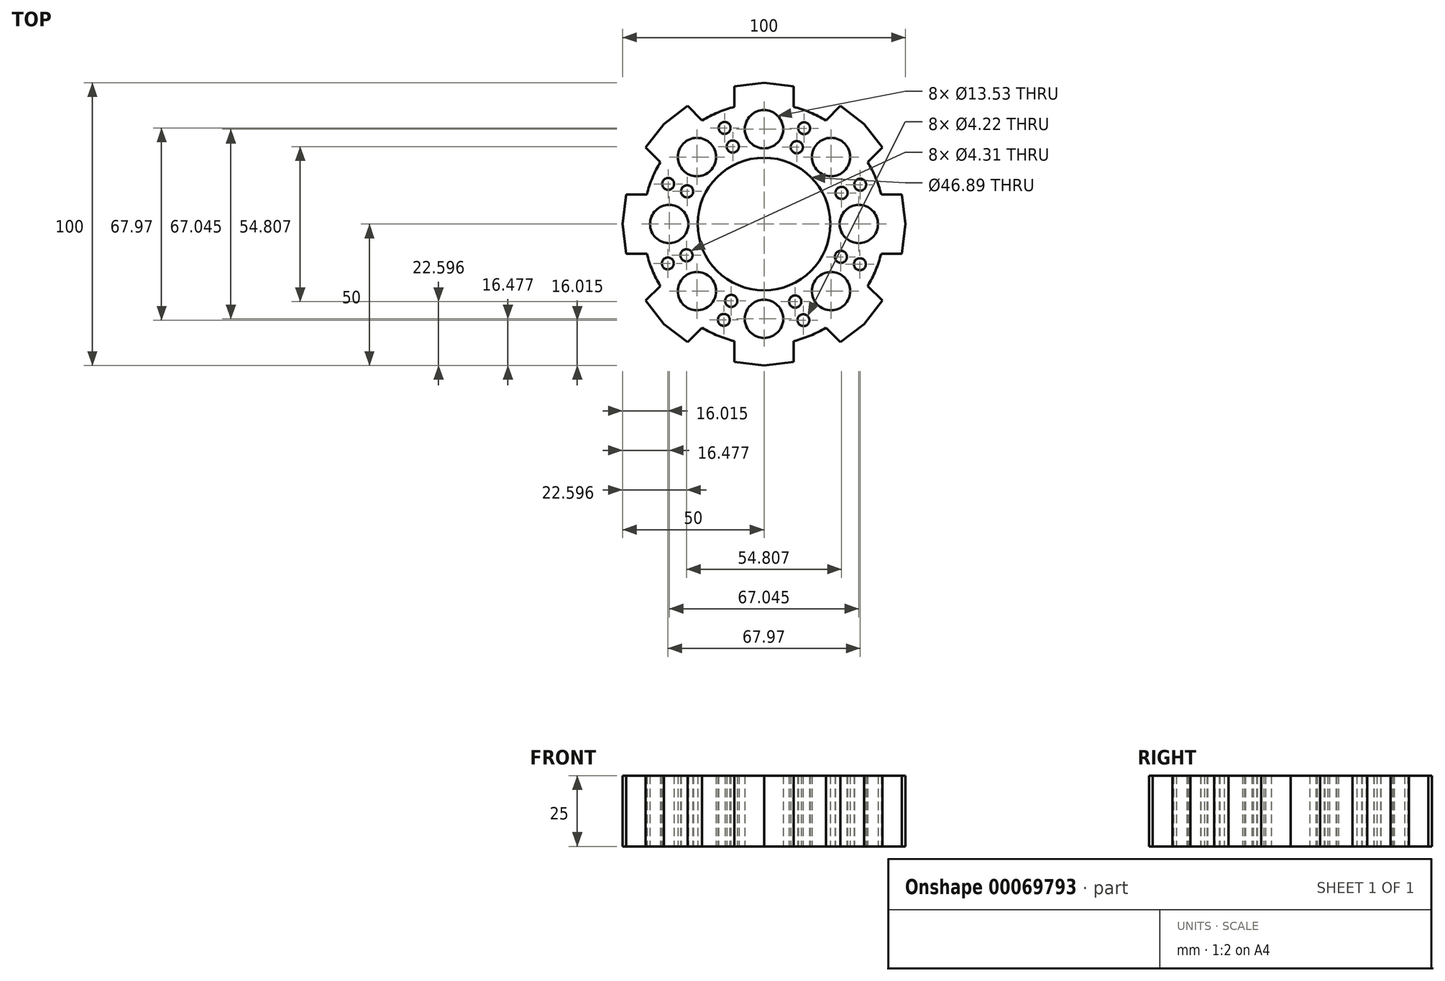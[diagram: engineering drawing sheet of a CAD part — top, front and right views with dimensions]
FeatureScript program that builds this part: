
annotation { "Feature Type Name" : "Feature", "Feature Type Description" : "" }
export const myFeature = defineFeature(function(context is Context, id is Id, definition is map)
    precondition{}
    {
        {
            var Q0;
            Q0=qCreatedBy(makeId("Top.planeOp"),FACE);
            var sketch = newSketch(context, id + "F0", { "sketchPlane" : qUnion([Q0])});
            skLineSegment(sketch, "E0", {"start": v(0, 0) * mm, "end": v(0, 50) * mm});
            skSolve(sketch);
        }
        {
            var Q0;
            Q0=qCreatedBy(makeId("Top.planeOp"),FACE);
            var sketch = newSketch(context, id + "F1", { "sketchPlane" : qUnion([Q0])});
            skLineSegment(sketch, "E1", {"start": v(0, 50) * mm, "end": v(10.44, 48.67) * mm});
            skLineSegment(sketch, "E2", {"start": v(10.44, 48.67) * mm, "end": v(10.44, 41.4) * mm});
            skArc(sketch, "E3", {"start": v(-36.66, 21.9) * mm, "mid": v(-39.45, 16.34) * mm, "end": v(-41.4, 10.44) * mm});
            skLineSegment(sketch, "E4.MirrorCS", {"start": v(0, 50) * mm, "end": v(-10.44, 48.67) * mm});
            skLineSegment(sketch, "E5.MirrorCS", {"start": v(-10.44, 48.67) * mm, "end": v(-10.44, 41.4) * mm});
            skLineSegment(sketch, "E6.1.0", {"start": v(-41.8, 27.03) * mm, "end": v(-36.66, 21.9) * mm});
            skLineSegment(sketch, "E6.1.1", {"start": v(-35.36, 35.36) * mm, "end": v(-41.8, 27.03) * mm});
            skLineSegment(sketch, "E6.1.2", {"start": v(-35.36, 35.36) * mm, "end": v(-27.03, 41.8) * mm});
            skLineSegment(sketch, "E6.1.3", {"start": v(-27.03, 41.8) * mm, "end": v(-21.9, 36.66) * mm});
            skLineSegment(sketch, "E6.2.0", {"start": v(-48.67, -10.44) * mm, "end": v(-41.4, -10.44) * mm});
            skLineSegment(sketch, "E6.2.1", {"start": v(-50, 0) * mm, "end": v(-48.67, -10.44) * mm});
            skLineSegment(sketch, "E6.2.2", {"start": v(-50, 0) * mm, "end": v(-48.67, 10.44) * mm});
            skLineSegment(sketch, "E6.2.3", {"start": v(-48.67, 10.44) * mm, "end": v(-41.4, 10.44) * mm});
            skLineSegment(sketch, "E6.3.0", {"start": v(-27.03, -41.8) * mm, "end": v(-21.9, -36.66) * mm});
            skLineSegment(sketch, "E6.3.1", {"start": v(-35.36, -35.36) * mm, "end": v(-27.03, -41.8) * mm});
            skLineSegment(sketch, "E6.3.2", {"start": v(-35.36, -35.36) * mm, "end": v(-41.8, -27.03) * mm});
            skLineSegment(sketch, "E6.3.3", {"start": v(-41.8, -27.03) * mm, "end": v(-36.66, -21.9) * mm});
            skLineSegment(sketch, "E6.4.0", {"start": v(10.44, -48.67) * mm, "end": v(10.44, -41.4) * mm});
            skLineSegment(sketch, "E6.4.1", {"start": v(0, -50) * mm, "end": v(10.44, -48.67) * mm});
            skLineSegment(sketch, "E6.4.2", {"start": v(0, -50) * mm, "end": v(-10.44, -48.67) * mm});
            skLineSegment(sketch, "E6.4.3", {"start": v(-10.44, -48.67) * mm, "end": v(-10.44, -41.4) * mm});
            skLineSegment(sketch, "E6.5.0", {"start": v(41.8, -27.03) * mm, "end": v(36.66, -21.9) * mm});
            skLineSegment(sketch, "E6.5.1", {"start": v(35.36, -35.36) * mm, "end": v(41.8, -27.03) * mm});
            skLineSegment(sketch, "E6.5.2", {"start": v(35.36, -35.36) * mm, "end": v(27.03, -41.8) * mm});
            skLineSegment(sketch, "E6.5.3", {"start": v(27.03, -41.8) * mm, "end": v(21.9, -36.66) * mm});
            skLineSegment(sketch, "E6.6.0", {"start": v(48.67, 10.44) * mm, "end": v(41.4, 10.44) * mm});
            skLineSegment(sketch, "E6.6.1", {"start": v(50, 0) * mm, "end": v(48.67, 10.44) * mm});
            skLineSegment(sketch, "E6.6.2", {"start": v(50, 0) * mm, "end": v(48.67, -10.44) * mm});
            skLineSegment(sketch, "E6.6.3", {"start": v(48.67, -10.44) * mm, "end": v(41.4, -10.44) * mm});
            skLineSegment(sketch, "E6.7.0", {"start": v(27.03, 41.8) * mm, "end": v(21.9, 36.66) * mm});
            skLineSegment(sketch, "E6.7.1", {"start": v(35.36, 35.36) * mm, "end": v(27.03, 41.8) * mm});
            skLineSegment(sketch, "E6.7.2", {"start": v(35.36, 35.36) * mm, "end": v(41.8, 27.03) * mm});
            skLineSegment(sketch, "E6.7.3", {"start": v(41.8, 27.03) * mm, "end": v(36.66, 21.9) * mm});
            skArc(sketch, "E7.trimOffspring", {"start": v(-41.4, -10.44) * mm, "mid": v(-39.45, -16.34) * mm, "end": v(-36.66, -21.9) * mm});
            skArc(sketch, "E8.trimOffspring", {"start": v(-21.9, -36.66) * mm, "mid": v(-16.34, -39.45) * mm, "end": v(-10.44, -41.4) * mm});
            skArc(sketch, "E9.trimOffspring", {"start": v(10.44, -41.4) * mm, "mid": v(16.34, -39.45) * mm, "end": v(21.9, -36.66) * mm});
            skArc(sketch, "E10.trimOffspring", {"start": v(36.66, -21.9) * mm, "mid": v(39.45, -16.34) * mm, "end": v(41.4, -10.44) * mm});
            skArc(sketch, "E11.trimOffspring", {"start": v(41.4, 10.44) * mm, "mid": v(39.45, 16.34) * mm, "end": v(36.66, 21.9) * mm});
            skArc(sketch, "E12.trimOffspring", {"start": v(21.9, 36.66) * mm, "mid": v(16.34, 39.45) * mm, "end": v(10.44, 41.4) * mm});
            skArc(sketch, "E13.trimOffspring", {"start": v(-10.44, 41.4) * mm, "mid": v(-16.34, 39.45) * mm, "end": v(-21.9, 36.66) * mm});
            skCircle(sketch, "E14", {"center": v(0, 0) * mm, "radius": 23.45 * mm});
            skCircle(sketch, "E15", {"center": v(0, 33.52) * mm, "radius": 6.77 * mm});
            skCircle(sketch, "E16.1.0", {"center": v(-23.7, 23.7) * mm, "radius": 6.77 * mm});
            skCircle(sketch, "E16.2.0", {"center": v(-33.52, 0) * mm, "radius": 6.77 * mm});
            skCircle(sketch, "E16.3.0", {"center": v(-23.7, -23.7) * mm, "radius": 6.77 * mm});
            skCircle(sketch, "E16.4.0", {"center": v(0, -33.52) * mm, "radius": 6.77 * mm});
            skCircle(sketch, "E16.5.0", {"center": v(23.7, -23.7) * mm, "radius": 6.77 * mm});
            skCircle(sketch, "E16.6.0", {"center": v(33.52, 0) * mm, "radius": 6.77 * mm});
            skCircle(sketch, "E16.7.0", {"center": v(23.7, 23.7) * mm, "radius": 6.77 * mm});
            skCircle(sketch, "E17", {"center": v(-13.92, 33.99) * mm, "radius": 2.1 * mm});
            skCircle(sketch, "E18", {"center": v(-11.03, 27.4) * mm, "radius": 2.15 * mm});
            skCircle(sketch, "E19.1.0", {"center": v(-33.87, 14.19) * mm, "radius": 2.1 * mm});
            skCircle(sketch, "E19.2.0", {"center": v(-33.99, -13.92) * mm, "radius": 2.1 * mm});
            skCircle(sketch, "E19.3.0", {"center": v(-14.19, -33.87) * mm, "radius": 2.1 * mm});
            skCircle(sketch, "E19.4.0", {"center": v(13.92, -33.99) * mm, "radius": 2.1 * mm});
            skCircle(sketch, "E19.5.0", {"center": v(33.87, -14.19) * mm, "radius": 2.1 * mm});
            skCircle(sketch, "E19.6.0", {"center": v(33.99, 13.92) * mm, "radius": 2.1 * mm});
            skCircle(sketch, "E19.7.0", {"center": v(14.19, 33.87) * mm, "radius": 2.1 * mm});
            skCircle(sketch, "E20.1.0", {"center": v(-27.17, 11.58) * mm, "radius": 2.15 * mm});
            skCircle(sketch, "E20.2.0", {"center": v(-27.4, -11.03) * mm, "radius": 2.15 * mm});
            skCircle(sketch, "E20.3.0", {"center": v(-11.58, -27.17) * mm, "radius": 2.15 * mm});
            skCircle(sketch, "E20.4.0", {"center": v(11.03, -27.4) * mm, "radius": 2.15 * mm});
            skCircle(sketch, "E20.5.0", {"center": v(27.17, -11.58) * mm, "radius": 2.15 * mm});
            skCircle(sketch, "E20.6.0", {"center": v(27.4, 11.03) * mm, "radius": 2.15 * mm});
            skCircle(sketch, "E20.7.0", {"center": v(11.58, 27.17) * mm, "radius": 2.15 * mm});
            skSolve(sketch);
        }
        {
            var Q0;
            Q0 = qSketchRegion(id + "F1", true);
            extrude(context, id + "F2", {"entities" : qUnion([Q0]), "endBound" : BoundingType.SYMMETRIC, "depth" : 25 * mm});
        }
    });
